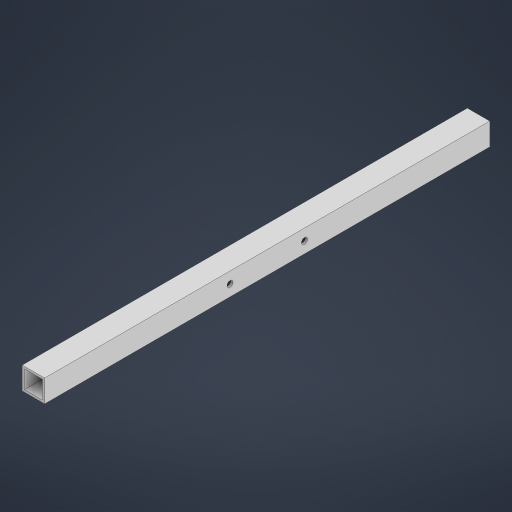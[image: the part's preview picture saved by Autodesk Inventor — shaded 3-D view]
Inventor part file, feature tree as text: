
AUTODESK INVENTOR PART (.ipt)
format: ipt  version: 2024 (Build 280153000, 153)  size: 186,368 bytes
history: native  units: mm
features: extrude x2, sketch x2, other x1
ambient origin geometry x8: Origin, YZ Plane, XZ Plane, XY Plane, X Axis, Y Axis, Z Axis, Center Point
bodies: Body1 (feature_tree)
feature tree (5):
  other  "Sólido1"
  extrude  "Extrusión1"  Depth=15.0mm
  extrude  "Extrusión2"  Depth=1.5mm
  sketch  "Boceto1"  dims[d0=15.0mm d1=15.0mm]
  sketch  "Boceto2"  dims[d2=1.5mm d3=1.5mm d4=1.5mm d5=1.5mm d6=298.4mm d7=0.0mm d8=4.0mm d9=4.0mm d10=7.5mm d11=7.5mm d12=50.0mm d13=124.2mm d14=10.0mm d15=0.0mm]
